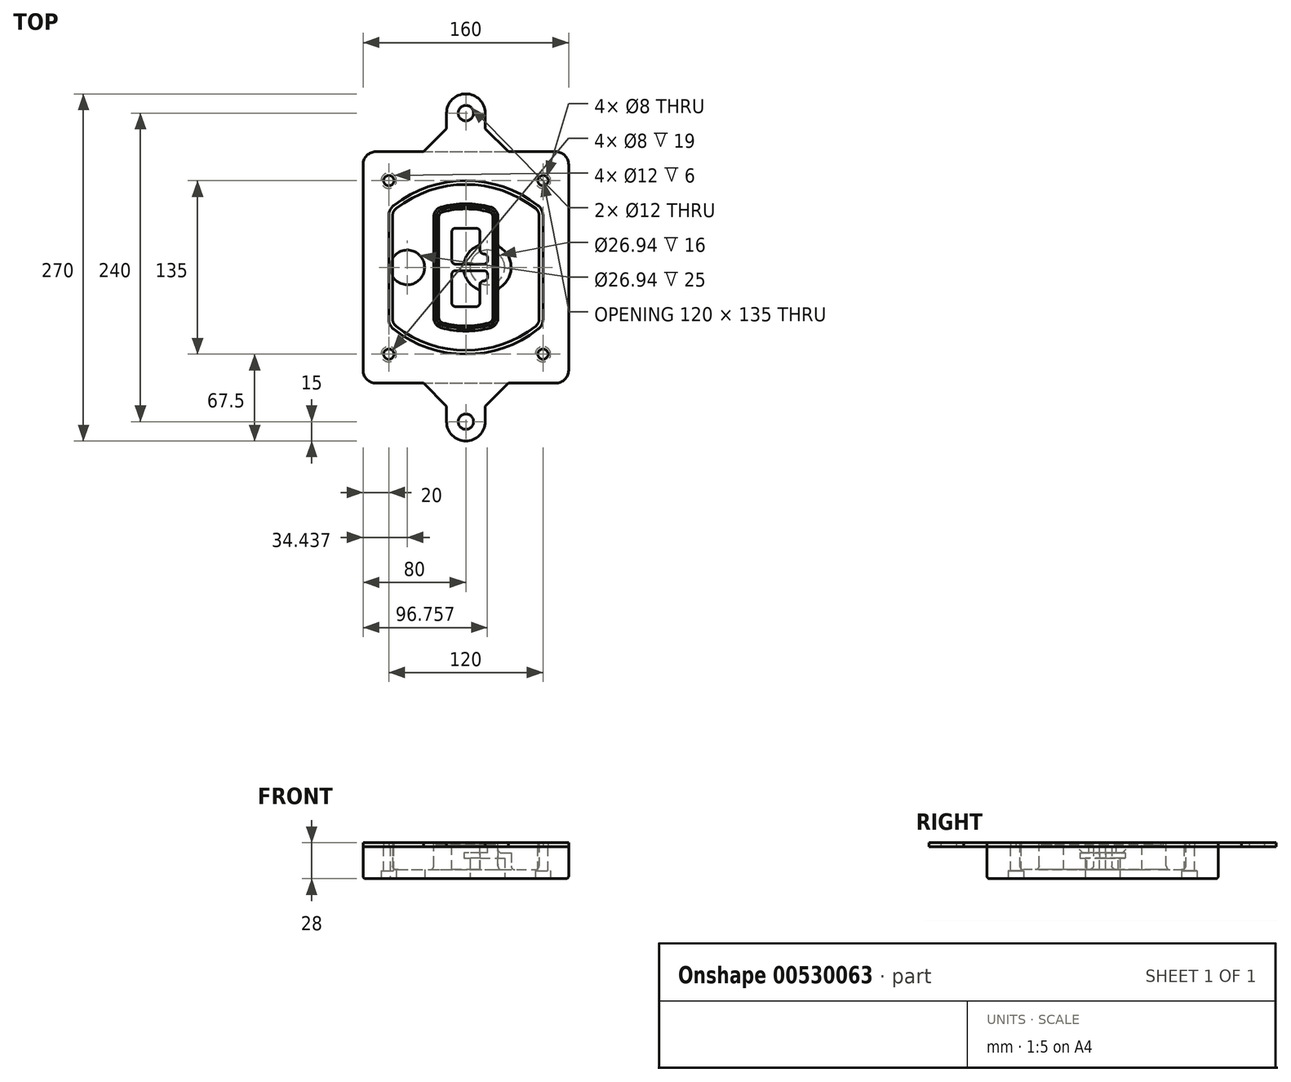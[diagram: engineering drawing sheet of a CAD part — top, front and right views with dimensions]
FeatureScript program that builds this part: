
annotation { "Feature Type Name" : "Feature", "Feature Type Description" : "" }
export const myFeature = defineFeature(function(context is Context, id is Id, definition is map)
    precondition{}
    {
        {
            var Q0;
            Q0=qCreatedBy(makeId("Top.planeOp"),FACE);
            var sketch = newSketch(context, id + "F0", { "sketchPlane" : qUnion([Q0])});
            skPoint(sketch, "E0.rect.middle", {"position": v(0, 0) * mm});
            skLineSegment(sketch, "E1.bottom", {"start": v(-70, -90) * mm, "end": v(70, -90) * mm});
            skLineSegment(sketch, "E1.top", {"start": v(-70, 90) * mm, "end": v(70, 90) * mm});
            skLineSegment(sketch, "E1.left", {"start": v(-80, -80) * mm, "end": v(-80, 80) * mm});
            skLineSegment(sketch, "E1.right", {"start": v(80, -80) * mm, "end": v(80, 80) * mm});
            skLineSegment(sketch, "E2", {"start": v(-80, 90) * mm, "end": v(80, -90) * mm, "construction": true});
            skLineSegment(sketch, "E3", {"start": v(80, 90) * mm, "end": v(-80, -90) * mm, "construction": true});
            skCircle(sketch, "E4", {"center": v(-60, 67.5) * mm, "radius": 4 * mm});
            skCircle(sketch, "E5", {"center": v(60, 67.5) * mm, "radius": 4 * mm});
            skCircle(sketch, "E6", {"center": v(60, -67.5) * mm, "radius": 4 * mm});
            skCircle(sketch, "E7", {"center": v(-60, -67.5) * mm, "radius": 4 * mm});
            skLineSegment(sketch, "E8", {"start": v(-60, 67.5) * mm, "end": v(60, 67.5) * mm, "construction": true});
            skLineSegment(sketch, "E9", {"start": v(60, 67.5) * mm, "end": v(60, -67.5) * mm, "construction": true});
            skLineSegment(sketch, "E10", {"start": v(60, -67.5) * mm, "end": v(-60, -67.5) * mm, "construction": true});
            skLineSegment(sketch, "E11", {"start": v(-60, -67.5) * mm, "end": v(-60, 67.5) * mm, "construction": true});
            skLineSegment(sketch, "E12", {"start": v(-60, 40.3) * mm, "end": v(-60, -40.3) * mm});
            skLineSegment(sketch, "E13", {"start": v(60, 40.3) * mm, "end": v(60, -40.3) * mm});
            skArc(sketch, "E14", {"start": v(56.15, 48.18) * mm, "mid": v(0, 67.5) * mm, "end": v(-56.15, 48.18) * mm});
            skArc(sketch, "E15", {"start": v(-56.15, -48.18) * mm, "mid": v(0, -67.5) * mm, "end": v(56.15, -48.18) * mm});
            skLineSegment(sketch, "E16", {"start": v(-60, 0) * mm, "end": v(60, 0) * mm, "construction": true});
            skPoint(sketch, "E17.visualSharp", {"position": v(-60, -45) * mm});
            skArc(sketch, "E17.filletArc", {"start": v(-60, -40.3) * mm, "mid": v(-58.99, -44.68) * mm, "end": v(-56.15, -48.18) * mm});
            skPoint(sketch, "E18.visualSharp", {"position": v(-60, 45) * mm});
            skArc(sketch, "E18.filletArc", {"start": v(-56.15, 48.18) * mm, "mid": v(-58.99, 44.68) * mm, "end": v(-60, 40.3) * mm});
            skPoint(sketch, "E19.visualSharp", {"position": v(60, 45) * mm});
            skArc(sketch, "E19.filletArc", {"start": v(60, 40.3) * mm, "mid": v(58.99, 44.68) * mm, "end": v(56.15, 48.18) * mm});
            skPoint(sketch, "E20.visualSharp", {"position": v(60, -45) * mm});
            skArc(sketch, "E20.filletArc", {"start": v(56.15, -48.18) * mm, "mid": v(58.99, -44.68) * mm, "end": v(60, -40.3) * mm});
            skPoint(sketch, "E21.visualSharp", {"position": v(-80, 90) * mm});
            skArc(sketch, "E21.filletArc", {"start": v(-70, 90) * mm, "mid": v(-77.07, 87.07) * mm, "end": v(-80, 80) * mm});
            skPoint(sketch, "E22.visualSharp", {"position": v(80, 90) * mm});
            skArc(sketch, "E22.filletArc", {"start": v(80, 80) * mm, "mid": v(77.07, 87.07) * mm, "end": v(70, 90) * mm});
            skPoint(sketch, "E23.visualSharp", {"position": v(80, -90) * mm});
            skArc(sketch, "E23.filletArc", {"start": v(70, -90) * mm, "mid": v(77.07, -87.07) * mm, "end": v(80, -80) * mm});
            skPoint(sketch, "E24.visualSharp", {"position": v(-80, -90) * mm});
            skArc(sketch, "E24.filletArc", {"start": v(-80, -80) * mm, "mid": v(-77.07, -87.07) * mm, "end": v(-70, -90) * mm});
            skArc(sketch, "E25.0", {"start": v(57, 40.3) * mm, "mid": v(56.3, 43.36) * mm, "end": v(54.3, 45.81) * mm});
            skLineSegment(sketch, "E25.1", {"start": v(57, 40.3) * mm, "end": v(57, -40.3) * mm});
            skArc(sketch, "E25.2", {"start": v(54.3, -45.81) * mm, "mid": v(56.3, -43.36) * mm, "end": v(57, -40.3) * mm});
            skArc(sketch, "E25.3", {"start": v(-54.3, -45.81) * mm, "mid": v(0, -64.5) * mm, "end": v(54.3, -45.81) * mm});
            skArc(sketch, "E25.4", {"start": v(-57, -40.3) * mm, "mid": v(-56.3, -43.36) * mm, "end": v(-54.3, -45.81) * mm});
            skArc(sketch, "E25.5", {"start": v(54.3, 45.81) * mm, "mid": v(0, 64.5) * mm, "end": v(-54.3, 45.81) * mm});
            skLineSegment(sketch, "E25.6", {"start": v(-57, 40.3) * mm, "end": v(-57, -40.3) * mm});
            skArc(sketch, "E25.7", {"start": v(-54.3, 45.81) * mm, "mid": v(-56.3, 43.36) * mm, "end": v(-57, 40.3) * mm});
            skArc(sketch, "E26.0", {"start": v(-58.62, 51.33) * mm, "mid": v(-62.58, 46.43) * mm, "end": v(-64, 40.3) * mm});
            skArc(sketch, "E26.1", {"start": v(58.62, 51.33) * mm, "mid": v(0, 71.5) * mm, "end": v(-58.62, 51.33) * mm});
            skArc(sketch, "E26.2", {"start": v(64, 40.3) * mm, "mid": v(62.58, 46.43) * mm, "end": v(58.62, 51.33) * mm});
            skLineSegment(sketch, "E26.3", {"start": v(64, 40.3) * mm, "end": v(64, -40.3) * mm});
            skArc(sketch, "E26.4", {"start": v(58.62, -51.33) * mm, "mid": v(62.58, -46.43) * mm, "end": v(64, -40.3) * mm});
            skLineSegment(sketch, "E26.5", {"start": v(-64, 40.3) * mm, "end": v(-64, -40.3) * mm});
            skArc(sketch, "E26.6", {"start": v(-58.62, -51.33) * mm, "mid": v(0, -71.5) * mm, "end": v(58.62, -51.33) * mm});
            skArc(sketch, "E26.7", {"start": v(-64, -40.3) * mm, "mid": v(-62.58, -46.43) * mm, "end": v(-58.62, -51.33) * mm});
            skSolve(sketch);
        }
        {
            var Q0;
            Q0=makeQuery(id+"F0.imprint","IMPRINT",FACE,{"disambiguationData":[TD([[makeQuery(id+"F0.imprint","IMPRINT",EDGE,{"derivedFrom":sQuery(id+"F0.wireOp",EDGE,"E1.bottom")}),1.0]])]});
            var Q1;
            Q1=makeQuery(id+"F0.imprint","IMPRINT",FACE,{"disambiguationData":[TD([[makeQuery(id+"F0.imprint","IMPRINT",EDGE,{"derivedFrom":sQuery(id+"F0.wireOp",EDGE,"E12")}),1.0]])]});
            var Q2;
            Q2=makeQuery(id+"F0.imprint","IMPRINT",FACE,{"disambiguationData":[TD([[makeQuery(id+"F0.imprint","IMPRINT",EDGE,{"derivedFrom":sQuery(id+"F0.wireOp",EDGE,"E25.0")}),1.0]])]});
            var Q3;
            Q3=makeQuery(id+"F0.imprint","IMPRINT",FACE,{"disambiguationData":[TD([[makeQuery(id+"F0.imprint","IMPRINT",EDGE,{"derivedFrom":sQuery(id+"F0.wireOp",EDGE,"E12")}),-1.0]])]});
            extrude(context, id + "F1", {"entities" : qUnion([Q0, Q1, Q2, Q3]), "oppositeDirection" : true, "depth" : 25 * mm});
        }
        {
            var Q0;
            Q0=makeQuery(id+"F0.imprint","IMPRINT",FACE,{"disambiguationData":[TD([[makeQuery(id+"F0.imprint","IMPRINT",EDGE,{"derivedFrom":sQuery(id+"F0.wireOp",EDGE,"E12")}),1.0]])]});
            extrude(context, id + "F2", {"entities" : qUnion([Q0]), "operationType" : NewBodyOperationType.ADD, "depth" : 3 * mm});
        }
        {
            var Q0;
            Q0=makeQuery(id+"F0.imprint","IMPRINT",FACE,{"disambiguationData":[TD([[makeQuery(id+"F0.imprint","IMPRINT",EDGE,{"derivedFrom":sQuery(id+"F0.wireOp",EDGE,"E25.0")}),1.0]])]});
            extrude(context, id + "F3", {"entities" : qUnion([Q0]), "operationType" : NewBodyOperationType.REMOVE, "oppositeDirection" : true, "depth" : 18 * mm});
        }
        {
            var Q0;
            Q0=makeQuery(id+"F2.opExtrude","CAP_FACE",FACE,{"disambiguationData":[OSD([sQuery(id+"F0.wireOp",EDGE,"E12"),sQuery(id+"F0.wireOp",EDGE,"E13"),sQuery(id+"F0.wireOp",EDGE,"E14"),sQuery(id+"F0.wireOp",EDGE,"E15"),sQuery(id+"F0.wireOp",EDGE,"E17.filletArc"),sQuery(id+"F0.wireOp",EDGE,"E18.filletArc"),sQuery(id+"F0.wireOp",EDGE,"E19.filletArc"),sQuery(id+"F0.wireOp",EDGE,"E20.filletArc"),sQuery(id+"F0.wireOp",EDGE,"E25.0"),sQuery(id+"F0.wireOp",EDGE,"E25.1"),sQuery(id+"F0.wireOp",EDGE,"E25.2"),sQuery(id+"F0.wireOp",EDGE,"E25.3"),sQuery(id+"F0.wireOp",EDGE,"E25.4"),sQuery(id+"F0.wireOp",EDGE,"E25.5"),sQuery(id+"F0.wireOp",EDGE,"E25.6"),sQuery(id+"F0.wireOp",EDGE,"E25.7")])],"isStart":false});
            var sketch = newSketch(context, id + "F4", { "sketchPlane" : qUnion([Q0])});
            skArc(sketch, "E27.0", {"start": v(-19.08, -46.97) * mm, "mid": v(0, -49.5) * mm, "end": v(19.08, -46.97) * mm});
            skArc(sketch, "E28.0", {"start": v(19.08, 46.97) * mm, "mid": v(0, 49.5) * mm, "end": v(-19.08, 46.97) * mm});
            skLineSegment(sketch, "E29", {"start": v(-25, 39.25) * mm, "end": v(-25, -39.25) * mm});
            skLineSegment(sketch, "E30", {"start": v(25, 39.25) * mm, "end": v(25, -39.25) * mm});
            skLineSegment(sketch, "E31", {"start": v(-25, 45.1) * mm, "end": v(25, 45.1) * mm, "construction": true});
            skLineSegment(sketch, "E32", {"start": v(-25, -45.1) * mm, "end": v(25, -45.1) * mm, "construction": true});
            skPoint(sketch, "E33.visualSharp", {"position": v(-25, 45.1) * mm});
            skArc(sketch, "E33.filletArc", {"start": v(-19.08, 46.97) * mm, "mid": v(-23.35, 44.11) * mm, "end": v(-25, 39.25) * mm});
            skPoint(sketch, "E34.visualSharp", {"position": v(25, 45.1) * mm});
            skArc(sketch, "E34.filletArc", {"start": v(25, 39.25) * mm, "mid": v(23.35, 44.11) * mm, "end": v(19.08, 46.97) * mm});
            skPoint(sketch, "E35.visualSharp", {"position": v(25, -45.1) * mm});
            skArc(sketch, "E35.filletArc", {"start": v(19.08, -46.97) * mm, "mid": v(23.35, -44.11) * mm, "end": v(25, -39.25) * mm});
            skPoint(sketch, "E36.visualSharp", {"position": v(-25, -45.1) * mm});
            skArc(sketch, "E36.filletArc", {"start": v(-25, -39.25) * mm, "mid": v(-23.35, -44.11) * mm, "end": v(-19.08, -46.97) * mm});
            skArc(sketch, "E37.0", {"start": v(54.3, 45.81) * mm, "mid": v(0, 64.5) * mm, "end": v(-54.3, 45.81) * mm});
            skArc(sketch, "E37.1", {"start": v(-54.3, 45.81) * mm, "mid": v(-56.3, 43.36) * mm, "end": v(-57, 40.3) * mm});
            skLineSegment(sketch, "E37.2", {"start": v(-57, 40.3) * mm, "end": v(-57, -40.3) * mm});
            skArc(sketch, "E37.3", {"start": v(-57, -40.3) * mm, "mid": v(-56.3, -43.36) * mm, "end": v(-54.3, -45.81) * mm});
            skArc(sketch, "E37.4", {"start": v(-54.3, -45.81) * mm, "mid": v(0, -64.5) * mm, "end": v(54.3, -45.81) * mm});
            skArc(sketch, "E37.5", {"start": v(54.3, -45.81) * mm, "mid": v(56.3, -43.36) * mm, "end": v(57, -40.3) * mm});
            skLineSegment(sketch, "E37.6", {"start": v(57, 40.3) * mm, "end": v(57, -40.3) * mm});
            skArc(sketch, "E37.7", {"start": v(57, 40.3) * mm, "mid": v(56.3, 43.36) * mm, "end": v(54.3, 45.81) * mm});
            skLineSegment(sketch, "E38.0", {"start": v(23, 39.25) * mm, "end": v(23, -39.25) * mm});
            skArc(sketch, "E38.1", {"start": v(18.56, -45.04) * mm, "mid": v(21.76, -42.9) * mm, "end": v(23, -39.25) * mm});
            skArc(sketch, "E38.2", {"start": v(-18.56, -45.04) * mm, "mid": v(0, -47.5) * mm, "end": v(18.56, -45.04) * mm});
            skArc(sketch, "E38.3", {"start": v(-23, -39.25) * mm, "mid": v(-21.76, -42.9) * mm, "end": v(-18.56, -45.04) * mm});
            skLineSegment(sketch, "E38.4", {"start": v(-23, 39.25) * mm, "end": v(-23, -39.25) * mm});
            skArc(sketch, "E38.5", {"start": v(23, 39.25) * mm, "mid": v(21.76, 42.9) * mm, "end": v(18.56, 45.04) * mm});
            skArc(sketch, "E38.6", {"start": v(-18.56, 45.04) * mm, "mid": v(-21.76, 42.9) * mm, "end": v(-23, 39.25) * mm});
            skArc(sketch, "E38.7", {"start": v(18.56, 45.04) * mm, "mid": v(0, 47.5) * mm, "end": v(-18.56, 45.04) * mm});
            skArc(sketch, "E39.0", {"start": v(21, 39.25) * mm, "mid": v(20.18, 41.68) * mm, "end": v(18.04, 43.1) * mm});
            skLineSegment(sketch, "E39.1", {"start": v(21, 39.25) * mm, "end": v(21, -39.25) * mm});
            skArc(sketch, "E39.2", {"start": v(18.04, -43.1) * mm, "mid": v(20.18, -41.68) * mm, "end": v(21, -39.25) * mm});
            skArc(sketch, "E39.3", {"start": v(-18.04, -43.1) * mm, "mid": v(0, -45.5) * mm, "end": v(18.04, -43.1) * mm});
            skArc(sketch, "E39.4", {"start": v(-21, -39.25) * mm, "mid": v(-20.18, -41.68) * mm, "end": v(-18.04, -43.1) * mm});
            skArc(sketch, "E39.5", {"start": v(18.04, 43.1) * mm, "mid": v(0, 45.5) * mm, "end": v(-18.04, 43.1) * mm});
            skLineSegment(sketch, "E39.6", {"start": v(-21, 39.25) * mm, "end": v(-21, -39.25) * mm});
            skArc(sketch, "E39.7", {"start": v(-18.04, 43.1) * mm, "mid": v(-20.18, 41.68) * mm, "end": v(-21, 39.25) * mm});
            skLineSegment(sketch, "E40", {"start": v(-25, 0) * mm, "end": v(25, 0) * mm, "construction": true});
            skLineSegment(sketch, "E41", {"start": v(-11, 5.5) * mm, "end": v(-11, 27.5) * mm});
            skLineSegment(sketch, "E42", {"start": v(-8, 30.5) * mm, "end": v(8, 30.5) * mm});
            skLineSegment(sketch, "E43", {"start": v(11, 27.5) * mm, "end": v(11, 13.5) * mm});
            skLineSegment(sketch, "E44", {"start": v(14, 10.5) * mm, "end": v(14, 10.5) * mm});
            skLineSegment(sketch, "E45", {"start": v(17, 7.5) * mm, "end": v(17, 5.5) * mm});
            skLineSegment(sketch, "E46", {"start": v(14, 2.5) * mm, "end": v(-8, 2.5) * mm});
            skPoint(sketch, "E47.visualSharp", {"position": v(-11, 30.5) * mm});
            skArc(sketch, "E47.filletArc", {"start": v(-8, 30.5) * mm, "mid": v(-10.12, 29.62) * mm, "end": v(-11, 27.5) * mm});
            skPoint(sketch, "E48.visualSharp", {"position": v(11, 30.5) * mm});
            skArc(sketch, "E48.filletArc", {"start": v(11, 27.5) * mm, "mid": v(10.12, 29.62) * mm, "end": v(8, 30.5) * mm});
            skPoint(sketch, "E49.visualSharp", {"position": v(11, 10.5) * mm});
            skArc(sketch, "E49.filletArc", {"start": v(11, 13.5) * mm, "mid": v(11.88, 11.38) * mm, "end": v(14, 10.5) * mm});
            skPoint(sketch, "E50.visualSharp", {"position": v(17, 10.5) * mm});
            skArc(sketch, "E50.filletArc", {"start": v(17, 7.5) * mm, "mid": v(16.12, 9.62) * mm, "end": v(14, 10.5) * mm});
            skPoint(sketch, "E51.visualSharp", {"position": v(17, 2.5) * mm});
            skArc(sketch, "E51.filletArc", {"start": v(14, 2.5) * mm, "mid": v(16.12, 3.38) * mm, "end": v(17, 5.5) * mm});
            skPoint(sketch, "E52.visualSharp", {"position": v(-11, 2.5) * mm});
            skArc(sketch, "E52.filletArc", {"start": v(-11, 5.5) * mm, "mid": v(-10.12, 3.38) * mm, "end": v(-8, 2.5) * mm});
            skLineSegment(sketch, "E53.0.MirrorCS", {"start": v(14, -2.5) * mm, "end": v(-8, -2.5) * mm});
            skArc(sketch, "E54.0.MirrorCS", {"start": v(-11, -5.5) * mm, "mid": v(-10.12, -3.38) * mm, "end": v(-8, -2.5) * mm});
            skLineSegment(sketch, "E55.0.MirrorCS", {"start": v(-11, -5.5) * mm, "end": v(-11, -27.5) * mm});
            skArc(sketch, "E56.0.MirrorCS", {"start": v(-8, -30.5) * mm, "mid": v(-10.12, -29.62) * mm, "end": v(-11, -27.5) * mm});
            skLineSegment(sketch, "E57.0.MirrorCS", {"start": v(-8, -30.5) * mm, "end": v(8, -30.5) * mm});
            skArc(sketch, "E58.0.MirrorCS", {"start": v(11, -27.5) * mm, "mid": v(10.12, -29.62) * mm, "end": v(8, -30.5) * mm});
            skLineSegment(sketch, "E59.0.MirrorCS", {"start": v(11, -27.5) * mm, "end": v(11, -13.5) * mm});
            skArc(sketch, "E60.0.MirrorCS", {"start": v(11, -13.5) * mm, "mid": v(11.88, -11.38) * mm, "end": v(14, -10.5) * mm});
            skArc(sketch, "E61.0.MirrorCS", {"start": v(17, -7.5) * mm, "mid": v(16.12, -9.62) * mm, "end": v(14, -10.5) * mm});
            skLineSegment(sketch, "E62.0.MirrorCS", {"start": v(17, -7.5) * mm, "end": v(17, -5.5) * mm});
            skArc(sketch, "E63.0.MirrorCS", {"start": v(14, -2.5) * mm, "mid": v(16.12, -3.38) * mm, "end": v(17, -5.5) * mm});
            skSolve(sketch);
        }
        {
            var Q0;
            Q0=makeQuery(id+"F4.imprint","IMPRINT",FACE,{"disambiguationData":[TD([[makeQuery(id+"F4.imprint","IMPRINT",EDGE,{"derivedFrom":sQuery(id+"F4.wireOp",EDGE,"E27.0")}),1.0]])]});
            var Q1;
            Q1=makeQuery(id+"F4.imprint","IMPRINT",FACE,{"disambiguationData":[TD([[makeQuery(id+"F4.imprint","IMPRINT",EDGE,{"derivedFrom":sQuery(id+"F4.wireOp",EDGE,"E38.0")}),-1.0]])]});
            var Q2;
            Q2=makeQuery(id+"F4.imprint","IMPRINT",FACE,{"disambiguationData":[TD([[makeQuery(id+"F4.imprint","IMPRINT",EDGE,{"derivedFrom":sQuery(id+"F4.wireOp",EDGE,"E39.0")}),1.0]])]});
            extrude(context, id + "F5", {"entities" : qUnion([Q0, Q1, Q2]), "operationType" : NewBodyOperationType.ADD, "endBound" : BoundingType.UP_TO_NEXT, "oppositeDirection" : true, "depth" : 25 * mm});
        }
        {
            var Q0;
            Q0=makeQuery(id+"F4.imprint","IMPRINT",FACE,{"disambiguationData":[TD([[makeQuery(id+"F4.imprint","IMPRINT",EDGE,{"derivedFrom":sQuery(id+"F4.wireOp",EDGE,"E38.0")}),-1.0]])]});
            extrude(context, id + "F6", {"entities" : qUnion([Q0]), "operationType" : NewBodyOperationType.REMOVE, "oppositeDirection" : true, "depth" : 2 * mm});
        }
        {
            var Q0;
            Q0=makeQuery(id+"F1.opExtrude","CAP_FACE",FACE,{"disambiguationData":[OSD([sQuery(id+"F0.wireOp",EDGE,"E1.bottom"),sQuery(id+"F0.wireOp",EDGE,"E1.top"),sQuery(id+"F0.wireOp",EDGE,"E1.left"),sQuery(id+"F0.wireOp",EDGE,"E1.right"),sQuery(id+"F0.wireOp",EDGE,"E4"),sQuery(id+"F0.wireOp",EDGE,"E5"),sQuery(id+"F0.wireOp",EDGE,"E6"),sQuery(id+"F0.wireOp",EDGE,"E7"),sQuery(id+"F0.wireOp",EDGE,"E21.filletArc"),sQuery(id+"F0.wireOp",EDGE,"E22.filletArc"),sQuery(id+"F0.wireOp",EDGE,"E23.filletArc"),sQuery(id+"F0.wireOp",EDGE,"E24.filletArc")])],"isStart":false});
            var sketch = newSketch(context, id + "F7", { "sketchPlane" : qUnion([Q0])});
            skCircle(sketch, "E64", {"center": v(16.76, 0) * mm, "radius": 13.47 * mm});
            skCircle(sketch, "E65", {"center": v(-45.56, 0) * mm, "radius": 13.47 * mm});
            skLineSegment(sketch, "E66", {"start": v(80, 0) * mm, "end": v(-80, 0) * mm});
            skCircle(sketch, "E67", {"center": v(16.76, 0) * mm, "radius": 18.47 * mm});
            skCircle(sketch, "E68", {"center": v(60, -67.5) * mm, "radius": 6 * mm});
            skCircle(sketch, "E69", {"center": v(-60, -67.5) * mm, "radius": 6 * mm});
            skCircle(sketch, "E70", {"center": v(-60, 67.5) * mm, "radius": 6 * mm});
            skCircle(sketch, "E71", {"center": v(60, 67.5) * mm, "radius": 6 * mm});
            skSolve(sketch);
        }
        {
            var Q0;
            {var subQ1=sQuery(id+"F7.wireOp",EDGE,"E66");var subQ4=sQuery(id+"F7.wireOp",EDGE,"E64");var subQ6=makeQuery(id+"F7.imprint","INTERSECT",VERTEX,{"disambiguationData":[OD(0.0)],"derivedFrom":[subQ4,subQ1]});Q0=makeQuery(id+"F7.imprint","IMPRINT",FACE,{"disambiguationData":[TD([[makeQuery(id+"F7.imprint","IMPRINT",EDGE,{"disambiguationData":[TD([[subQ6,-1.0]])],"derivedFrom":subQ4}),-1.0]])]});}
            var Q1;
            {var subQ0=sQuery(id+"F7.wireOp",EDGE,"E66");var subQ1=sQuery(id+"F7.wireOp",EDGE,"E64");var subQ3=makeQuery(id+"F7.imprint","INTERSECT",VERTEX,{"disambiguationData":[OD(0.0)],"derivedFrom":[subQ1,subQ0]});Q1=makeQuery(id+"F7.imprint","IMPRINT",FACE,{"disambiguationData":[TD([[makeQuery(id+"F7.imprint","IMPRINT",EDGE,{"disambiguationData":[TD([[subQ3,-1.0]])],"derivedFrom":subQ1}),1.0]])]});}
            var Q2;
            {var subQ0=sQuery(id+"F7.wireOp",EDGE,"E66");var subQ1=sQuery(id+"F7.wireOp",EDGE,"E64");var subQ3=makeQuery(id+"F7.imprint","INTERSECT",VERTEX,{"disambiguationData":[OD(0.0)],"derivedFrom":[subQ1,subQ0]});Q2=makeQuery(id+"F7.imprint","IMPRINT",FACE,{"disambiguationData":[TD([[makeQuery(id+"F7.imprint","IMPRINT",EDGE,{"disambiguationData":[TD([[subQ3,1.0]])],"derivedFrom":subQ1}),1.0]])]});}
            var Q3;
            {var subQ1=sQuery(id+"F7.wireOp",EDGE,"E66");var subQ4=sQuery(id+"F7.wireOp",EDGE,"E64");var subQ6=makeQuery(id+"F7.imprint","INTERSECT",VERTEX,{"disambiguationData":[OD(0.0)],"derivedFrom":[subQ4,subQ1]});Q3=makeQuery(id+"F7.imprint","IMPRINT",FACE,{"disambiguationData":[TD([[makeQuery(id+"F7.imprint","IMPRINT",EDGE,{"disambiguationData":[TD([[subQ6,1.0]])],"derivedFrom":subQ4}),-1.0]])]});}
            extrude(context, id + "F8", {"entities" : qUnion([Q0, Q1, Q2, Q3]), "operationType" : NewBodyOperationType.ADD, "oppositeDirection" : true, "depth" : 20 * mm});
        }
        {
            var Q0;
            {var subQ0=sQuery(id+"F7.wireOp",EDGE,"E66");var subQ1=sQuery(id+"F7.wireOp",EDGE,"E64");var subQ3=makeQuery(id+"F7.imprint","INTERSECT",VERTEX,{"disambiguationData":[OD(0.0)],"derivedFrom":[subQ1,subQ0]});Q0=makeQuery(id+"F7.imprint","IMPRINT",FACE,{"disambiguationData":[TD([[makeQuery(id+"F7.imprint","IMPRINT",EDGE,{"disambiguationData":[TD([[subQ3,-1.0]])],"derivedFrom":subQ1}),1.0]])]});}
            var Q1;
            {var subQ0=sQuery(id+"F7.wireOp",EDGE,"E66");var subQ1=sQuery(id+"F7.wireOp",EDGE,"E64");var subQ3=makeQuery(id+"F7.imprint","INTERSECT",VERTEX,{"disambiguationData":[OD(0.0)],"derivedFrom":[subQ1,subQ0]});Q1=makeQuery(id+"F7.imprint","IMPRINT",FACE,{"disambiguationData":[TD([[makeQuery(id+"F7.imprint","IMPRINT",EDGE,{"disambiguationData":[TD([[subQ3,1.0]])],"derivedFrom":subQ1}),1.0]])]});}
            extrude(context, id + "F9", {"entities" : qUnion([Q0, Q1]), "operationType" : NewBodyOperationType.REMOVE, "oppositeDirection" : true, "depth" : 16 * mm});
        }
        {
            var Q0;
            {var subQ0=sQuery(id+"F7.wireOp",EDGE,"E66");var subQ1=sQuery(id+"F7.wireOp",EDGE,"E65");var subQ3=makeQuery(id+"F7.imprint","INTERSECT",VERTEX,{"disambiguationData":[OD(0.0)],"derivedFrom":[subQ1,subQ0]});Q0=makeQuery(id+"F7.imprint","IMPRINT",FACE,{"disambiguationData":[TD([[makeQuery(id+"F7.imprint","IMPRINT",EDGE,{"disambiguationData":[TD([[subQ3,-1.0]])],"derivedFrom":subQ1}),1.0]])]});}
            var Q1;
            {var subQ0=sQuery(id+"F7.wireOp",EDGE,"E66");var subQ1=sQuery(id+"F7.wireOp",EDGE,"E65");var subQ3=makeQuery(id+"F7.imprint","INTERSECT",VERTEX,{"disambiguationData":[OD(0.0)],"derivedFrom":[subQ1,subQ0]});Q1=makeQuery(id+"F7.imprint","IMPRINT",FACE,{"disambiguationData":[TD([[makeQuery(id+"F7.imprint","IMPRINT",EDGE,{"disambiguationData":[TD([[subQ3,1.0]])],"derivedFrom":subQ1}),1.0]])]});}
            extrude(context, id + "F10", {"entities" : qUnion([Q0, Q1]), "operationType" : NewBodyOperationType.REMOVE, "oppositeDirection" : true, "depth" : 25 * mm});
        }
        {
            var Q0;
            Q0=makeQuery(id+"F7.imprint","IMPRINT",FACE,{"disambiguationData":[TD([[makeQuery(id+"F7.imprint","IMPRINT",EDGE,{"derivedFrom":sQuery(id+"F7.wireOp",EDGE,"E68")}),1.0]])]});
            var Q1;
            Q1=makeQuery(id+"F7.imprint","IMPRINT",FACE,{"disambiguationData":[TD([[makeQuery(id+"F7.imprint","IMPRINT",EDGE,{"derivedFrom":makeQuery(id+"F1.opExtrude","CAP_EDGE",EDGE,{"disambiguationData":[OSD([sQuery(id+"F0.wireOp",EDGE,"E5")])],"isStart":false})}),-1.0]])]});
            var Q2;
            Q2=makeQuery(id+"F7.imprint","IMPRINT",FACE,{"disambiguationData":[TD([[makeQuery(id+"F7.imprint","IMPRINT",EDGE,{"derivedFrom":sQuery(id+"F7.wireOp",EDGE,"E69")}),1.0]])]});
            var Q3;
            Q3=makeQuery(id+"F7.imprint","IMPRINT",FACE,{"disambiguationData":[TD([[makeQuery(id+"F7.imprint","IMPRINT",EDGE,{"derivedFrom":makeQuery(id+"F1.opExtrude","CAP_EDGE",EDGE,{"disambiguationData":[OSD([sQuery(id+"F0.wireOp",EDGE,"E4")])],"isStart":false})}),-1.0]])]});
            var Q4;
            Q4=makeQuery(id+"F7.imprint","IMPRINT",FACE,{"disambiguationData":[TD([[makeQuery(id+"F7.imprint","IMPRINT",EDGE,{"derivedFrom":sQuery(id+"F7.wireOp",EDGE,"E70")}),1.0]])]});
            var Q5;
            Q5=makeQuery(id+"F7.imprint","IMPRINT",FACE,{"disambiguationData":[TD([[makeQuery(id+"F7.imprint","IMPRINT",EDGE,{"derivedFrom":makeQuery(id+"F1.opExtrude","CAP_EDGE",EDGE,{"disambiguationData":[OSD([sQuery(id+"F0.wireOp",EDGE,"E7")])],"isStart":false})}),-1.0]])]});
            var Q6;
            Q6=makeQuery(id+"F7.imprint","IMPRINT",FACE,{"disambiguationData":[TD([[makeQuery(id+"F7.imprint","IMPRINT",EDGE,{"derivedFrom":sQuery(id+"F7.wireOp",EDGE,"E71")}),1.0]])]});
            var Q7;
            Q7=makeQuery(id+"F7.imprint","IMPRINT",FACE,{"disambiguationData":[TD([[makeQuery(id+"F7.imprint","IMPRINT",EDGE,{"derivedFrom":makeQuery(id+"F1.opExtrude","CAP_EDGE",EDGE,{"disambiguationData":[OSD([sQuery(id+"F0.wireOp",EDGE,"E6")])],"isStart":false})}),-1.0]])]});
            extrude(context, id + "F11", {"entities" : qUnion([Q0, Q1, Q2, Q3, Q4, Q5, Q6, Q7]), "operationType" : NewBodyOperationType.REMOVE, "oppositeDirection" : true, "depth" : 6 * mm});
        }
        {
            var Q0;
            Q0=makeQuery(id+"F9.boolean.opBoolean","COPY",FACE,{"derivedFrom":makeQuery(id+"F9.opExtrude","CAP_FACE",FACE,{"disambiguationData":[OSD([sQuery(id+"F7.wireOp",EDGE,"E64")])],"isStart":false})});
            var sketch = newSketch(context, id + "F12", { "sketchPlane" : qUnion([Q0])});
            skArc(sketch, "E72.0", {"start": v(11, 17.55) * mm, "mid": v(2.57, 11.82) * mm, "end": v(-1.54, 2.5) * mm});
            skArc(sketch, "E72.1", {"start": v(-1.54, -2.5) * mm, "mid": v(2.57, -11.82) * mm, "end": v(11, -17.55) * mm});
            skLineSegment(sketch, "E73", {"start": v(-1.54, -2.5) * mm, "end": v(14, -2.5) * mm});
            skLineSegment(sketch, "E74.0", {"start": v(14, 2.5) * mm, "end": v(-1.54, 2.5) * mm});
            skArc(sketch, "E74.1", {"start": v(14, 2.5) * mm, "mid": v(16.12, 3.38) * mm, "end": v(17, 5.5) * mm});
            skLineSegment(sketch, "E74.2", {"start": v(17, 7.5) * mm, "end": v(17, 5.5) * mm});
            skArc(sketch, "E74.3", {"start": v(17, 7.5) * mm, "mid": v(16.12, 9.62) * mm, "end": v(14, 10.5) * mm});
            skArc(sketch, "E74.4", {"start": v(11, 13.5) * mm, "mid": v(11.88, 11.38) * mm, "end": v(14, 10.5) * mm});
            skLineSegment(sketch, "E74.5", {"start": v(11, 17.55) * mm, "end": v(11, 13.5) * mm});
            skLineSegment(sketch, "E74.7", {"start": v(14, -2.5) * mm, "end": v(-1.54, -2.5) * mm});
            skArc(sketch, "E74.8", {"start": v(14, -2.5) * mm, "mid": v(16.12, -3.38) * mm, "end": v(17, -5.5) * mm});
            skLineSegment(sketch, "E74.9", {"start": v(17, -7.5) * mm, "end": v(17, -5.5) * mm});
            skArc(sketch, "E74.10", {"start": v(17, -7.5) * mm, "mid": v(16.12, -9.62) * mm, "end": v(14, -10.5) * mm});
            skArc(sketch, "E74.11", {"start": v(11, -13.5) * mm, "mid": v(11.88, -11.38) * mm, "end": v(14, -10.5) * mm});
            skLineSegment(sketch, "E74.12", {"start": v(11, -17.55) * mm, "end": v(11, -13.5) * mm});
            skPoint(sketch, "E75.orphan", {"position": v(11, -27.5) * mm});
            skPoint(sketch, "E76.orphan", {"position": v(-8, -2.5) * mm});
            skPoint(sketch, "E77.orphan", {"position": v(-8, 2.5) * mm});
            skPoint(sketch, "E78.orphan", {"position": v(11, 27.5) * mm});
            skSolve(sketch);
        }
        {
            var Q0;
            {var subQ7=sQuery(id+"F12.wireOp",EDGE,"E72.0");var subQ14=sQuery(id+"F12.wireOp",EDGE,"E72.1");var subQ16=sQuery(id+"F12.wireOp",EDGE,"E74.1");var subQ18=sQuery(id+"F12.wireOp",EDGE,"E74.8");Q0=qUnion([makeQuery(id+"F12.imprint","IMPRINT",FACE,{"disambiguationData":[TD([[makeQuery(id+"F12.imprint","IMPRINT",EDGE,{"derivedFrom":subQ7}),1.0]])]}),makeQuery(id+"F12.imprint","IMPRINT",FACE,{"disambiguationData":[TD([[makeQuery(id+"F12.imprint","IMPRINT",EDGE,{"derivedFrom":subQ14}),1.0]])]}),makeQuery(id+"F12.imprint","IMPRINT",FACE,{"disambiguationData":[TD([[makeQuery(id+"F12.imprint","IMPRINT",EDGE,{"derivedFrom":subQ16}),1.0]])]}),makeQuery(id+"F12.imprint","IMPRINT",FACE,{"disambiguationData":[TD([[makeQuery(id+"F12.imprint","IMPRINT",EDGE,{"derivedFrom":subQ18}),-1.0]])]})]);}
            var Q1;
            Q1=makeQuery(id+"F5.boolean.opBoolean","SPLIT",FACE,{"disambiguationData":[TD([makeQuery(id+"F5.opExtrude","SWEPT_FACE",FACE,{"disambiguationData":[OSD([sQuery(id+"F4.wireOp",EDGE,"E41")])]})])],"derivedFrom":makeQuery(id+"F3.boolean.opBoolean","COPY",FACE,{"derivedFrom":makeQuery(id+"F3.opExtrude","CAP_FACE",FACE,{"disambiguationData":[OSD([sQuery(id+"F0.wireOp",EDGE,"E25.0"),sQuery(id+"F0.wireOp",EDGE,"E25.1"),sQuery(id+"F0.wireOp",EDGE,"E25.2"),sQuery(id+"F0.wireOp",EDGE,"E25.3"),sQuery(id+"F0.wireOp",EDGE,"E25.4"),sQuery(id+"F0.wireOp",EDGE,"E25.5"),sQuery(id+"F0.wireOp",EDGE,"E25.6"),sQuery(id+"F0.wireOp",EDGE,"E25.7")])],"isStart":false})})});
            extrude(context, id + "F13", {"entities" : qUnion([Q0]), "operationType" : NewBodyOperationType.REMOVE, "endBound" : BoundingType.UP_TO_SURFACE, "endBoundEntityFace" : qUnion([Q1]), "depth" : 25 * mm});
        }
        {
            var Q0;
            Q0=makeQuery(id+"F3.boolean.opBoolean","COPY",EDGE,{"derivedFrom":makeQuery(id+"F3.opExtrude","CAP_EDGE",EDGE,{"disambiguationData":[OSD([sQuery(id+"F0.wireOp",EDGE,"E25.6")])],"isStart":false})});
            var Q1;
            Q1=makeQuery(id+"F8.boolean.opBoolean","INTERSECT",EDGE,{"derivedFrom":[makeQuery(id+"F5.opExtrude","SWEPT_FACE",FACE,{"disambiguationData":[OSD([sQuery(id+"F4.wireOp",EDGE,"E30")])]}),makeQuery(id+"F8.opExtrude","CAP_FACE",FACE,{"disambiguationData":[OSD([sQuery(id+"F7.wireOp",EDGE,"E67")])],"isStart":false})]});
            var Q2;
            Q2=makeQuery(id+"F8.boolean.opBoolean","INTERSECT",EDGE,{"disambiguationData":[OD(1.0)],"derivedFrom":[makeQuery(id+"F5.opExtrude","SWEPT_FACE",FACE,{"disambiguationData":[OSD([sQuery(id+"F4.wireOp",EDGE,"E30")])]}),makeQuery(id+"F8.opExtrude","SWEPT_FACE",FACE,{"disambiguationData":[OSD([sQuery(id+"F7.wireOp",EDGE,"E67")])]})]});
            var Q3;
            {var subQ0=sQuery(id+"F4.wireOp",EDGE,"E30");Q3=makeQuery(id+"F8.boolean.opBoolean","SPLIT",EDGE,{"disambiguationData":[TD([makeQuery(id+"F5.opExtrude","SWEPT_FACE",FACE,{"disambiguationData":[OSD([sQuery(id+"F4.wireOp",EDGE,"E35.filletArc")])]})])],"derivedFrom":makeQuery(id+"F5.opExtrude","CAP_EDGE",EDGE,{"disambiguationData":[OSD([subQ0])],"isStart":false})});}
            var Q4;
            {var subQ0=sQuery(id+"F0.wireOp",EDGE,"E25.7");var subQ1=sQuery(id+"F0.wireOp",EDGE,"E25.1");var subQ2=sQuery(id+"F0.wireOp",EDGE,"E25.6");var subQ3=sQuery(id+"F0.wireOp",EDGE,"E25.5");var subQ4=sQuery(id+"F0.wireOp",EDGE,"E25.4");var subQ5=sQuery(id+"F0.wireOp",EDGE,"E25.0");var subQ6=sQuery(id+"F0.wireOp",EDGE,"E25.2");var subQ7=sQuery(id+"F0.wireOp",EDGE,"E25.3");Q4=makeQuery(id+"F8.boolean.opBoolean","INTERSECT",EDGE,{"derivedFrom":[makeQuery(id+"F5.boolean.opBoolean","SPLIT",FACE,{"disambiguationData":[TD([makeQuery(id+"F2.opExtrude","SWEPT_FACE",FACE,{"disambiguationData":[OSD([subQ5])]})])],"derivedFrom":makeQuery(id+"F3.boolean.opBoolean","COPY",FACE,{"derivedFrom":makeQuery(id+"F3.opExtrude","CAP_FACE",FACE,{"disambiguationData":[OSD([subQ5,subQ1,subQ6,subQ7,subQ4,subQ3,subQ2,subQ0])],"isStart":false})})}),makeQuery(id+"F8.opExtrude","SWEPT_FACE",FACE,{"disambiguationData":[OSD([sQuery(id+"F7.wireOp",EDGE,"E67")])]})]});}
            var Q5;
            Q5=makeQuery(id+"F8.boolean.opBoolean","INTERSECT",EDGE,{"disambiguationData":[OD(0.0)],"derivedFrom":[makeQuery(id+"F5.opExtrude","SWEPT_FACE",FACE,{"disambiguationData":[OSD([sQuery(id+"F4.wireOp",EDGE,"E30")])]}),makeQuery(id+"F8.opExtrude","SWEPT_FACE",FACE,{"disambiguationData":[OSD([sQuery(id+"F7.wireOp",EDGE,"E67")])]})]});
            fillet(context, id + "F14", {"entities" : qUnion([Q0, Q1, Q2, Q3, Q4, Q5]), "radius" : 3 * mm, "tangentPropagation" : true, "allowEdgeOverflow" : false});
        }
        {
            var Q0;
            Q0=makeQuery(id+"F1.opExtrude","CAP_EDGE",EDGE,{"disambiguationData":[OSD([sQuery(id+"F0.wireOp",EDGE,"E1.bottom")])],"isStart":false});
            fillet(context, id + "F15", {"entities" : qUnion([Q0]), "radius" : 2 * mm, "tangentPropagation" : true, "allowEdgeOverflow" : false});
        }
        {
            var Q0;
            {var subQ0=sQuery(id+"F0.wireOp",EDGE,"E21.filletArc");var subQ1=sQuery(id+"F0.wireOp",EDGE,"E7");var subQ2=sQuery(id+"F0.wireOp",EDGE,"E6");var subQ3=sQuery(id+"F0.wireOp",EDGE,"E5");var subQ4=sQuery(id+"F0.wireOp",EDGE,"E4");var subQ5=sQuery(id+"F0.wireOp",EDGE,"E22.filletArc");var subQ6=sQuery(id+"F0.wireOp",EDGE,"E1.bottom");var subQ7=sQuery(id+"F0.wireOp",EDGE,"E1.right");var subQ8=sQuery(id+"F0.wireOp",EDGE,"E1.top");var subQ9=sQuery(id+"F0.wireOp",EDGE,"E1.left");var subQ10=sQuery(id+"F0.wireOp",EDGE,"E23.filletArc");var subQ11=sQuery(id+"F0.wireOp",EDGE,"E24.filletArc");Q0=makeQuery(id+"F2.boolean.opBoolean","SPLIT",FACE,{"disambiguationData":[TD([makeQuery(id+"F1.opExtrude","SWEPT_FACE",FACE,{"disambiguationData":[OSD([subQ6])]})])],"derivedFrom":makeQuery(id+"F1.opExtrude","CAP_FACE",FACE,{"disambiguationData":[OSD([subQ6,subQ8,subQ9,subQ7,subQ4,subQ3,subQ2,subQ1,subQ0,subQ5,subQ10,subQ11])],"isStart":true})});}
            var sketch = newSketch(context, id + "F16", { "sketchPlane" : qUnion([Q0])});
            skLineSegment(sketch, "E79", {"start": v(0, 90) * mm, "end": v(0, 120) * mm, "construction": true});
            skCircle(sketch, "E80", {"center": v(0, 120) * mm, "radius": 6 * mm});
            skLineSegment(sketch, "E81", {"start": v(-33, 90) * mm, "end": v(-15, 108) * mm});
            skLineSegment(sketch, "E82", {"start": v(-15, 108) * mm, "end": v(-15, 120) * mm});
            skLineSegment(sketch, "E83", {"start": v(33, 90) * mm, "end": v(15, 108) * mm});
            skLineSegment(sketch, "E84", {"start": v(15, 108) * mm, "end": v(15, 120) * mm});
            skArc(sketch, "E85", {"start": v(15, 120) * mm, "mid": v(0, 135) * mm, "end": v(-15, 120) * mm});
            skLineSegment(sketch, "E86", {"start": v(0, 120) * mm, "end": v(15, 120) * mm, "construction": true});
            skLineSegment(sketch, "E87", {"start": v(0, 120) * mm, "end": v(-15, 120) * mm, "construction": true});
            skLineSegment(sketch, "E88", {"start": v(80, 0) * mm, "end": v(-80, 0) * mm, "construction": true});
            skLineSegment(sketch, "E89.MirrorCS", {"start": v(33, -90) * mm, "end": v(15, -108) * mm});
            skLineSegment(sketch, "E90.MirrorCS", {"start": v(15, -108) * mm, "end": v(15, -120) * mm});
            skArc(sketch, "E91.MirrorCS", {"start": v(15, -120) * mm, "mid": v(0, -135) * mm, "end": v(-15, -120) * mm});
            skCircle(sketch, "E92.MirrorC", {"center": v(0, -120) * mm, "radius": 6 * mm});
            skLineSegment(sketch, "E93.MirrorCS", {"start": v(0, -90) * mm, "end": v(0, -120) * mm, "construction": true});
            skLineSegment(sketch, "E94.MirrorCS", {"start": v(-33, -90) * mm, "end": v(-15, -108) * mm});
            skLineSegment(sketch, "E95.MirrorCS", {"start": v(-15, -108) * mm, "end": v(-15, -120) * mm});
            skSolve(sketch);
        }
        {
            var Q0;
            Q0=makeQuery(id+"F16.imprint","IMPRINT",FACE,{"disambiguationData":[TD([[makeQuery(id+"F16.imprint","IMPRINT",EDGE,{"derivedFrom":sQuery(id+"F16.wireOp",EDGE,"E80")}),-1.0]])]});
            var Q1;
            {var subQ0=sQuery(id+"F16.wireOp",EDGE,"E89.MirrorCS");Q1=makeQuery(id+"F16.imprint","IMPRINT",FACE,{"disambiguationData":[TD([[makeQuery(id+"F16.imprint","IMPRINT",EDGE,{"derivedFrom":subQ0}),-1.0]])]});}
            var Q2;
            Q2=makeQuery(id+"F16.imprint","IMPRINT",FACE,{"disambiguationData":[TD([[makeQuery(id+"F16.imprint","IMPRINT",EDGE,{"derivedFrom":makeQuery(id+"F1.opExtrude","CAP_EDGE",EDGE,{"disambiguationData":[OSD([sQuery(id+"F0.wireOp",EDGE,"E1.left")])],"isStart":true})}),-1.0]])]});
            var Q3;
            Q3=makeQuery(id+"F2.opExtrude","CAP_FACE",FACE,{"disambiguationData":[OSD([sQuery(id+"F0.wireOp",EDGE,"E12"),sQuery(id+"F0.wireOp",EDGE,"E13"),sQuery(id+"F0.wireOp",EDGE,"E14"),sQuery(id+"F0.wireOp",EDGE,"E15"),sQuery(id+"F0.wireOp",EDGE,"E17.filletArc"),sQuery(id+"F0.wireOp",EDGE,"E18.filletArc"),sQuery(id+"F0.wireOp",EDGE,"E19.filletArc"),sQuery(id+"F0.wireOp",EDGE,"E20.filletArc"),sQuery(id+"F0.wireOp",EDGE,"E25.0"),sQuery(id+"F0.wireOp",EDGE,"E25.1"),sQuery(id+"F0.wireOp",EDGE,"E25.2"),sQuery(id+"F0.wireOp",EDGE,"E25.3"),sQuery(id+"F0.wireOp",EDGE,"E25.4"),sQuery(id+"F0.wireOp",EDGE,"E25.5"),sQuery(id+"F0.wireOp",EDGE,"E25.6"),sQuery(id+"F0.wireOp",EDGE,"E25.7")])],"isStart":false});
            extrude(context, id + "F17", {"entities" : qUnion([Q0, Q1, Q2]), "endBound" : BoundingType.UP_TO_SURFACE, "depth" : 25 * mm, "endBoundEntityFace" : qUnion([Q3]), "offsetDistance" : 25 * mm});
        }
    });
